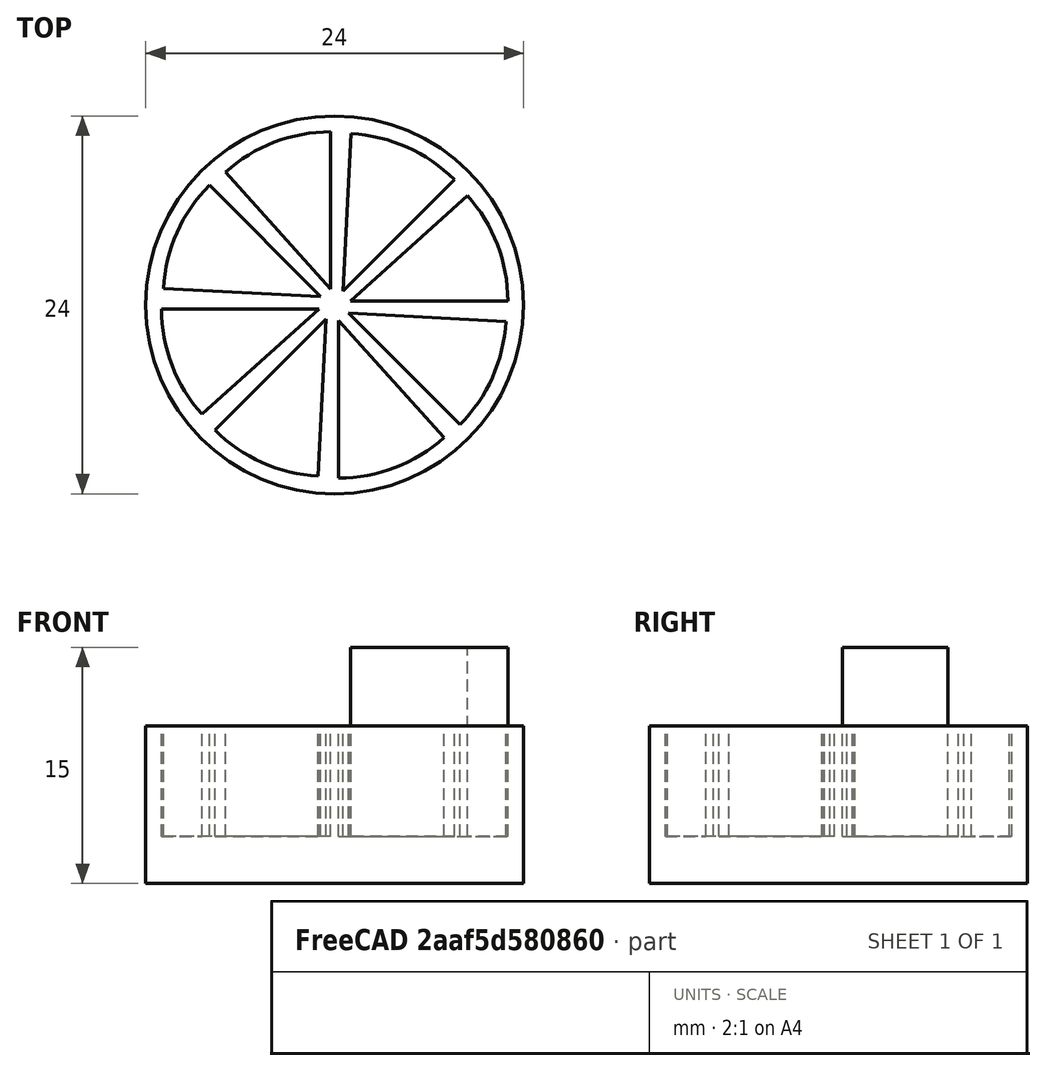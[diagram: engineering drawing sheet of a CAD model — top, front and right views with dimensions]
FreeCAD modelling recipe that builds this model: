
FCSTD DOCUMENT  (FreeCAD 1.0R39285 (Git))
Label: ojt1_t11r02_trivial
License: All rights reserved
objects: Part::Cylinder×2, Part::FeaturePython×1, Part::Cut×1
note: 3 computed .brp shape members not serialized (recipe doc carries the construction recipe); baked Part::Feature solids carry a one-line shape summary decoded from their .brp

FEATURE [Part::Cylinder] Cylinder  label="Cilindre"
  Angle = 360
  AttacherType = Attacher::AttachEngine3D
  FirstAngle = 0
  Height = 10
  Radius = 12
  SecondAngle = 0
FEATURE [Part::Cylinder] Cylinder001  label="Cilindre001"
  Angle = 42
  AttacherType = Attacher::AttachEngine3D
  FirstAngle = 0
  Height = 12
  Placement = pos=(1,0.25,3) rot=(0,0,1;0rad)
  Radius = 10
  SecondAngle = 0
FEATURE [Part::FeaturePython] Array  # Draft array (typed FeaturePython)
  AlwaysSyncPlacement = false
  Angle = 360
  ArrayType = 1
  Axis = (0,0,1)
  Base = -> Cylinder001
  Center = (0,0,0)
  Count = 8
  ExpandArray = false
  Fuse = false
  IntervalAxis = (0,0,0)
  IntervalX = (50,0,0)
  IntervalY = (0,50,0)
  IntervalZ = (0,0,50)
  NumberCircles = 3
  NumberPolar = 8
  NumberX = 2
  NumberY = 2
  NumberZ = 1
  PlacementList = 8 placements: [(1,0.25,3),(0.53033,0.883883,3),(-0.25,1,3),(-0.883883,0.53033,3),(-1,-0.25,3),(-0.53033,-0.883883,3),(0.25,-1,3),(0.883883,-0.53033,3)]
  RadialDistance = 50
  ScaleList = (8) [(1,1,1),(1,1,1),(1,1,1),(1,1,1),(1,1,1),(1,1,1),(1,1,1),(1,1,1)]
  Symmetry = 1
  TangentialDistance = 25
FEATURE [Part::Cut] Cut
  Base = -> Cylinder
  Refine = true
  Tool = -> Array
